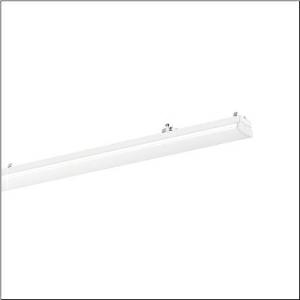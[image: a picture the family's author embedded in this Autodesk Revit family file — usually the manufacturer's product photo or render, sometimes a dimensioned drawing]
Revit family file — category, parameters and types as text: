
# Revit family: licross_r__21_recessed_opal_ho_52tl1ddn4e5m_042d
name_source: partatom
category: Lighting Fixtures
units: mm (PartAtom-declared; Revit-internal decimal feet)

## family parameters
Cut with Voids When Loaded = No
Host = Face
Light Source = No
Part Type = Normal
Room Calculation Point = No
Round Connector Dimension = Use Diameter
Shared = No

## types (1)
- --- (1 x LED, 14560 lm, 84.6 W, 4000K)
    Apparent Load = 85 VA
    CIE Flux Codes = 44 73 91 87 100
    Color Rendering = 80
    Color Temperature = 4000K
    Default Elevation = 1800 mm
    Description = Licross® 21 recessed opal HO, luminaire insert, of sheet steel, galvanised, coil coated, white, length: 1.500mm, width: 66mm, height: 67mm, LED rated luminous flux: 14.560lm, light colour: 840, control gear: DALI 2, with plug, 5-pole, with phase selection, mains connection: 220..240V, AC, 50/60Hz, rated input power: 85W, internal wiring halogen-free, primary optical cover: cover, of PMMA, light emission: direct with ceiling illumination distribution, primary light characteristic: symmetric, protection rating (complete): IP40, insulation class (complete): insulation class I (protective earthing), certification: CE, ENEC, VDE, UKCA, protection symbol: D if used in an environment without relevant dust loads with corresponding accessories, impact resistance: IK06, permissible ambient temperature for indoor applications: -25..+30°C, corresponds to IFS (International Featured Standards) requirements for safety and quality in the food industry, reducing of maximum allowable ambient temperature of 5°C with ceiling mounting, LABS conformity tested according to VDMA 24364:2018-05, packaging unit: 1 piece
    Height = 83 mm
    Lamp = 1 x LED
    Lamp Light Flux = 14560 lm
    Lamp Power = 84.6 W
    Lamp count = 1
    Length = 1500 mm
    Luminous efficacy = 172 lm/W
    Manufacturer = Siteco
    ModVariant = No
    Model = 52TL1DDN4E5M
    Mounting Place = Ceiling
    Mounting Type = Pendant
    Number of Poles = 1
    OnlyDefault = Yes
    Power Factor = 1
    Product Name = Licross® 21 recessed opal HO
    Product group = luminaire insert | ceiling pendant
    ProductGroupID = 902
    Protection Class = Protection class I
    Protection Degree = IP 40
    RLX_Detail_Level = 1
    RLX_Emergency_Light_Flux = 0 lm
    RLX_Emergency_Type = 0
    RLX_Emergency_Type_DB = No
    RlxData = <blob elided: 26973 chars, md5=4dfafbc3>
    Socket = socket
    Standby Power = 0 W
    System Light Flux = 14560 lm
    System Power = 85 W
    Type Comments = factory setting: luminous flux: 100 % | dim-lin: 254 | 484 mA
    Type Image = l_1313666.jpg
    URL = http://relux.com
    VarID = @adj_090069
    Voltage = 0 V
    Weight = 0.00 kg
    Width = 76 mm

## geometry (parser evidence)
native form markers: Blend x4, Sweep x13
no freeform markers — native parametric forms only
